FCSTD DOCUMENT  (FreeCAD 0.16R)
Label: 9thob
License: All rights reserved
LicenseURL: http://en.wikipedia.org/wiki/All_rights_reserved
objects: Sketcher::SketchObject×1
note: 1 computed .brp shape members not serialized (recipe doc carries the construction recipe); baked Part::Feature solids carry a one-line shape summary decoded from their .brp

FEATURE [Sketcher::SketchObject] Sketch
  sketch-geometry (7):
    g0: Circle CenterX=-88.9037 CenterY=49.0891 CenterZ=0 NormalX=0 NormalY=0 NormalZ=1 Radius=25.1576
    g1: ArcOfCircle CenterX=5.188 CenterY=14.2539 CenterZ=0 NormalX=0 NormalY=0 NormalZ=1 Radius=4.026 StartAngle=3.14159 EndAngle=4.36332
    g2: ArcOfCircle CenterX=-5.188 CenterY=14.2539 CenterZ=0 NormalX=0 NormalY=0 NormalZ=1 Radius=6.35 StartAngle=5.66859 EndAngle=8.20305
    g3: LineSegment [constr] StartX=0 StartY=0 StartZ=0 EndX=47.806 EndY=131.346 EndZ=0
    g4: LineSegment [constr] StartX=0 StartY=0 StartZ=0 EndX=-41.3219 EndY=113.531 EndZ=0
    g5: LineSegment [constr] StartX=-5.188 StartY=14.2539 StartZ=0 EndX=5.188 EndY=14.2539 EndZ=0
    g6: LineSegment [constr] StartX=0 StartY=27.4866 StartZ=0 EndX=0 EndY=0 EndZ=0
  constraints (18):
    c: Coincident(g3,g-1)
    c: Coincident(g4,g-1)
    c: PointOnObject(g5,g3)
    c: Radius(g1) = 4.026
    c: Coincident(g1,g5)
    c: Radius(g2) = 6.35
    c: Coincident(g6,g-1)
    c: Symmetric(g2,g1,g6)
    c: Tangent(g1,g2)
    c: Perpendicular(g6,g5)
    c: PointOnObject(g6,g-2)
    c: Coincident(g5,g2)
    c: PointOnObject(g2,g4)
    c: Angle(g3,g4) = 0.698132
    c: PointOnObject(g1,g5)
    c: PointOnObject(g1,g3)
    c: PointOnObject(g2,g6)
    c: PointOnObject(g2,g4)
